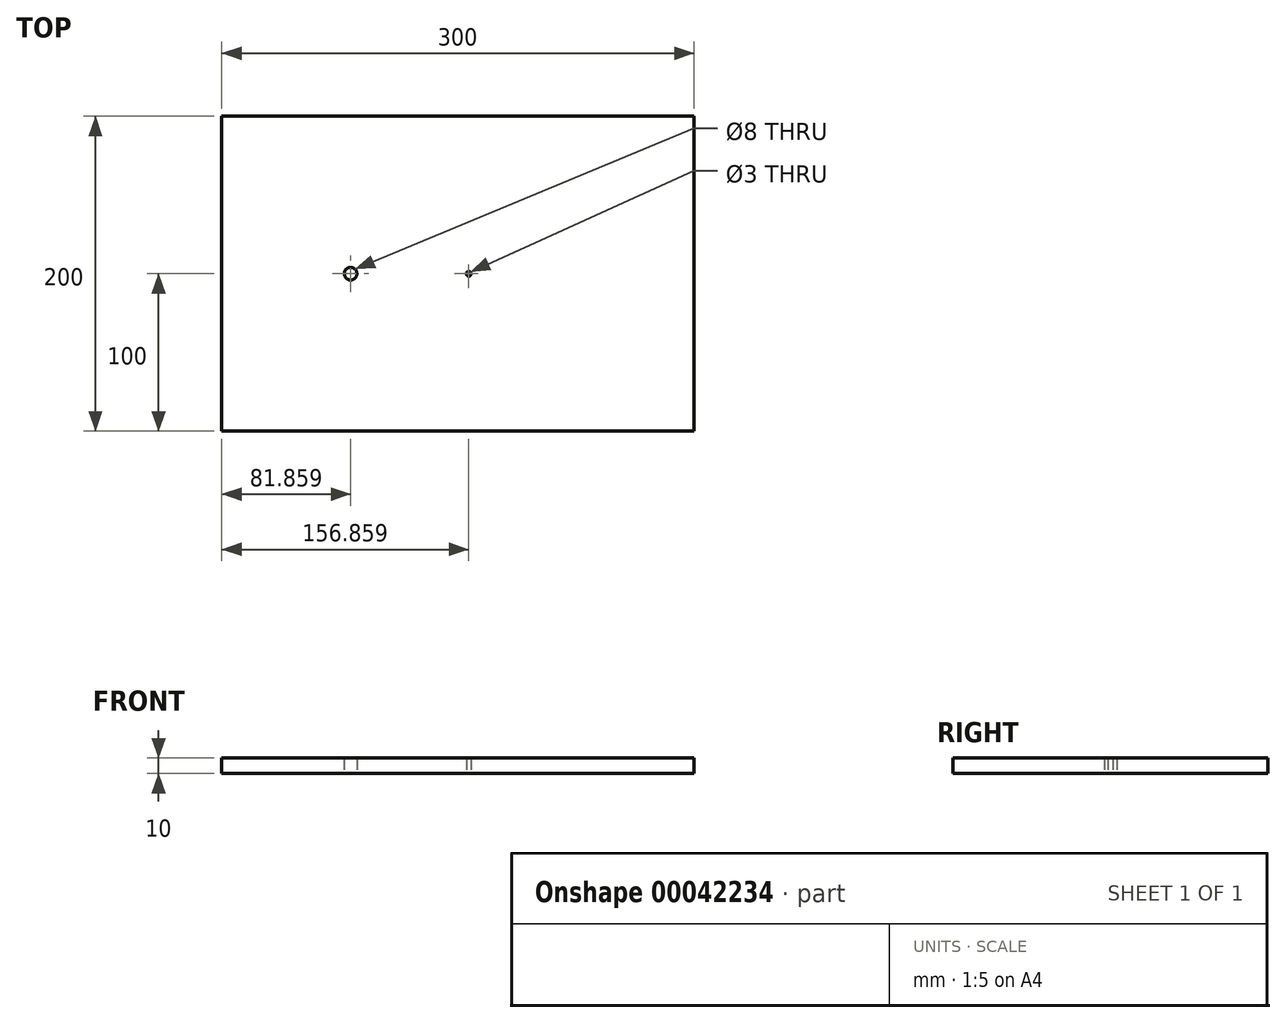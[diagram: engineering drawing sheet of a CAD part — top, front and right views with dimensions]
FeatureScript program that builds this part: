
annotation { "Feature Type Name" : "Feature", "Feature Type Description" : "" }
export const myFeature = defineFeature(function(context is Context, id is Id, definition is map)
    precondition{}
    {
        {
            var Q0;
            Q0=qCreatedBy(makeId("Top.planeOp"),FACE);
            var sketch = newSketch(context, id + "F0", { "sketchPlane" : qUnion([Q0])});
            skLineSegment(sketch, "E0.rect.bottom", {"start": v(150, -100) * mm, "end": v(-150, -100) * mm});
            skLineSegment(sketch, "E0.rect.top", {"start": v(150, 100) * mm, "end": v(-150, 100) * mm});
            skLineSegment(sketch, "E0.rect.left", {"start": v(150, -100) * mm, "end": v(150, 100) * mm});
            skLineSegment(sketch, "E0.rect.right", {"start": v(-150, -100) * mm, "end": v(-150, 100) * mm});
            skPoint(sketch, "E0.rect.middle", {"position": v(0, 0) * mm});
            skCircle(sketch, "E1", {"center": v(-68.14, 0) * mm, "radius": 4 * mm});
            skLineSegment(sketch, "E2", {"start": v(-68.14, 0) * mm, "end": v(6.86, 0) * mm});
            skCircle(sketch, "E3", {"center": v(6.86, 0) * mm, "radius": 1.5 * mm});
            skSolve(sketch);
        }
        {
            var Q0;
            Q0=makeQuery(id+"F0.imprint","IMPRINT",FACE,{"disambiguationData":[TD([[makeQuery(id+"F0.imprint","IMPRINT",EDGE,{"derivedFrom":sQuery(id+"F0.wireOp",EDGE,"E0.rect.bottom")}),-1.0]])]});
            extrude(context, id + "F1", {"entities" : qUnion([Q0]), "depth" : 10 * mm});
        }
    });
